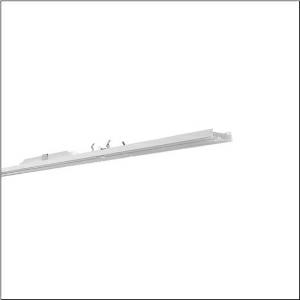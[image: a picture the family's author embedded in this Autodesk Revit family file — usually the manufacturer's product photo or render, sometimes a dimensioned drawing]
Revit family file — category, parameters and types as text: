
# Revit family: licross_r__11_recessed_ho_51ul1edv4m5r_686d
name_source: partatom
category: Lighting Fixtures
units: mm (PartAtom-declared; Revit-internal decimal feet)

## family parameters
Cut with Voids When Loaded = No
Host = Face
Light Source = No
Part Type = Normal
Room Calculation Point = No
Round Connector Dimension = Use Diameter
Shared = No

## types (1)
- --- (1 x LED, 25560 lm, 150.1 W, 4000K)
    Apparent Load = 150 VA
    CIE Flux Codes = 85 95 99 100 100
    Color Rendering = 80
    Color Temperature = 4000K
    Default Elevation = 1800 mm
    Description = Licross® 11 Recessed HO, luminaire insert, of sheet steel, galvanised, coil coated, white, length: 2.250mm, width: 66mm, height: 67mm, LED rated luminous flux: 25.560lm, light colour: 840, control gear: DALI 2, control gear: ECG DALI, with terminal, 5-pole, max. 2.5mm², mains connection: 230V, AC, 50/60Hz, halogen-free wiring, primary optical cover: cover, of PMMA, light emission: direct distribution, primary light characteristic: symmetric, protection rating (complete): IP40, insulation class (complete): insulation class I (protective earthing), certification: CE, ENEC, VDE, UKCA, protection symbol: D if used in an environment without relevant dust loads with corresponding accessories, permissible ambient temperature for indoor applications: -35..+35°C, corresponds to IFS (International Featured Standards) requirements for safety and quality in the food industry, reducing of maximum allowable ambient temperature of 5°C with ceiling mounting, LABS conformity tested according to VDMA 24364:2018-05, packaging unit: 1 piece
    Height = 58 mm
    Lamp = 1 x LED
    Lamp Light Flux = 25560 lm
    Lamp Power = 150.1 W
    Lamp count = 1
    Length = 2250 mm
    Luminous efficacy = 170 lm/W
    Manufacturer = Siteco
    ModVariant = No
    Model = 51UL1EDV4M5R
    Mounting Place = Ceiling
    Mounting Type = Pendant
    Number of Poles = 1
    OnlyDefault = Yes
    Power Factor = 1
    Product Name = Licross® 11 Recessed HO
    Product group = luminaire insert
    ProductGroupID = 902
    Protection Class = Protection class I
    Protection Degree = IP 40
    RLX_Detail_Level = 1
    RlxData = <blob elided: 26853 chars, md5=ab3bcf30>
    Socket = socket
    Standby Power = 0 W
    System Light Flux = 25561 lm
    System Power = 150 W
    Type Comments = factory setting: luminous flux: 100 % | dim-lin: 254 | 575 mA
    Type Image = l_1006953.jpg
    URL = http://relux.com
    VarID = @adj_092503
    Voltage = 0 V
    Weight = 0.00 kg
    Width = 66 mm

## geometry (parser evidence)
native form markers: Blend x4, Sweep x11
no freeform markers — native parametric forms only
